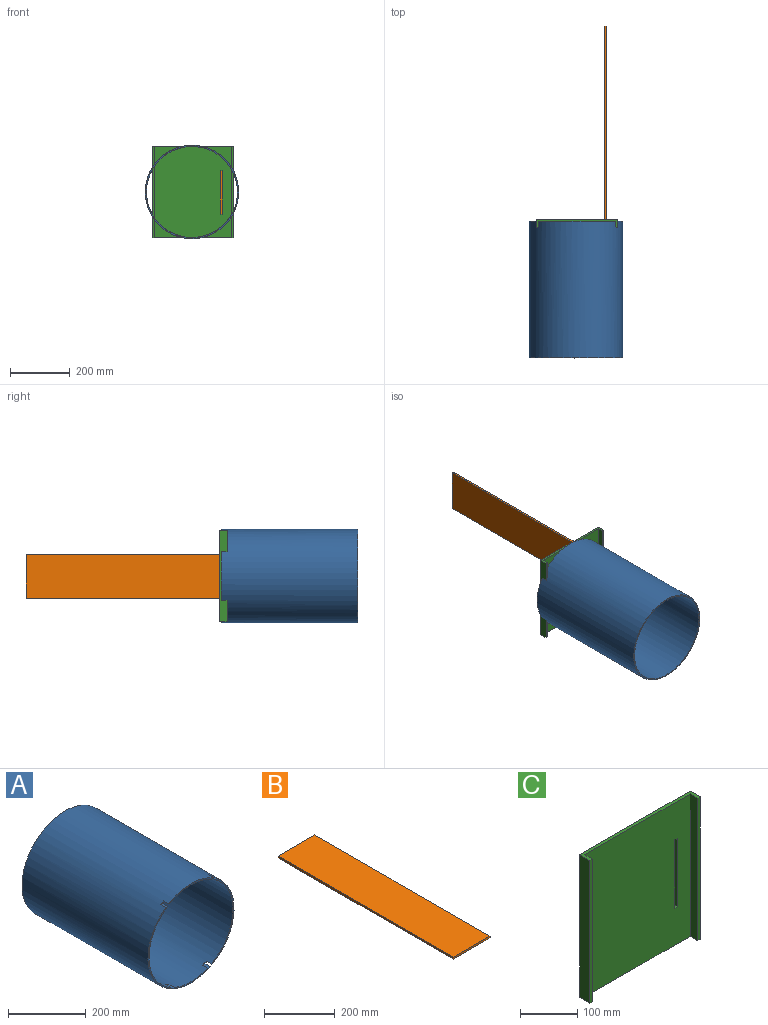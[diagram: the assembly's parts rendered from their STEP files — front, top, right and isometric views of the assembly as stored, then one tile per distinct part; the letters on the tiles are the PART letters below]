
ASSEMBLY  parts=3 mates=2
PART A: 19 faces, bbox 312.4x457.2x312.4 mm
  f0: cylinder r=152.4mm len=457.2mm, axis (0,1,0), area 436781.8mm2, adj f1,f2,f3,f4,f6,f7,f8,f9
  f1: plane 162.72x22.86mm, normal (0,-1,0), area 619.8mm2, adj f0,f5,f8,f16
  f2: plane 260.35x82.43mm, normal (0,-1,0), area 1182mm2, adj f0,f5,f11,f17
  f3: plane 260.35x82.43mm, normal (0,-1,0), area 1182mm2, adj f0,f5,f9,f13
  f4: plane 139.79x16.51mm, normal (0,-1,0), area 515.4mm2, adj f0,f5,f10,f14
  f5: cylinder r=156.21mm len=457.2mm, axis (0,1,0), area 447802.3mm2, adj f1,f2,f3,f4,f6,f7,f8,f9
  f6: plane 312.42x312.42mm, normal (0,1,0), area 3693.9mm2, adj f0,f5
  f7: plane 17.17x6.35mm, normal (0,-1,0), area 45.2mm2, adj f0,f5,f8,f9
  f8: plane 19.05x7.58mm, normal (0,0,-1), area 144.4mm2, adj f0,f1,f5,f7
  f9: plane 19.05x6.71mm, normal (0,0,1), area 127.9mm2, adj f0,f3,f5,f7
  f10: plane 19.05x8.99mm, normal (0,0,1), area 171.2mm2, adj f0,f4,f5,f12
  f11: plane 19.05x7.58mm, normal (0,0,-1), area 144.4mm2, adj f0,f2,f5,f12
  f12: plane 20.45x6.35mm, normal (0,-1,0), area 52.2mm2, adj f0,f5,f10,f11
  f13: plane 19.05x7.58mm, normal (0,0,-1), area 144.4mm2, adj f0,f3,f5,f15
  f14: plane 19.05x8.99mm, normal (0,0,1), area 171.2mm2, adj f0,f4,f5,f15
  f15: plane 20.45x6.35mm, normal (0,-1,0), area 52.2mm2, adj f0,f5,f13,f14
  f16: plane 19.05x7.58mm, normal (0,0,-1), area 144.4mm2, adj f0,f1,f5,f18
  f17: plane 19.05x6.71mm, normal (0,0,1), area 127.9mm2, adj f0,f2,f5,f18
  f18: plane 17.17x6.35mm, normal (0,-1,0), area 45.2mm2, adj f0,f5,f16,f17
PART B: 8 faces, bbox 146.1x698.5x6.4 mm
  f0: plane 698.5x6.35mm, normal (-1,0,0), area 4422.6mm2, adj f1,f3,f4,f5,f6,f7
  f1: plane 647.7x146.05mm, normal (0,0,-1), area 94596.6mm2, adj f0,f2,f4,f7
  f2: plane 698.5x6.35mm, normal (1,0,0), area 4422.6mm2, adj f1,f3,f4,f5,f6,f7
  f3: plane 698.5x146.05mm, normal (0,0,1), area 102015.9mm2, adj f0,f2,f4,f5
  f4: plane 146.05x6.35mm, normal (0,-1,0), area 927.4mm2, adj f0,f1,f2,f3
  f5: plane 146.05x6.1mm, normal (0,1,0), area 890.3mm2, adj f0,f2,f3,f6
  f6: plane 146.05x50.8mm, normal (0,0,-1), area 7419.3mm2, adj f0,f2,f5,f7
  f7: plane 146.05x0.25mm, normal (0,1,0), area 37.1mm2, adj f0,f1,f2,f6
PART C: 14 faces, bbox 273.1x25.4x304.8 mm
  f0: plane 304.8x260.35mm, normal (0,-1,0), area 78464.4mm2, adj f2,f4,f6,f8,f10,f11,f12,f13
  f1: plane 304.8x25.4mm, normal (-1,0,0), area 7741.9mm2, adj f2,f4,f5,f7
  f2: plane 273.05x25.4mm, normal (0,0,-1), area 1975.8mm2, adj f0,f1,f3,f5,f6,f7,f8,f9
  f3: plane 304.8x25.4mm, normal (1,0,0), area 7741.9mm2, adj f2,f4,f5,f9
  f4: plane 273.05x25.4mm, normal (0,0,1), area 1975.8mm2, adj f0,f1,f3,f5,f6,f7,f8,f9
  f5: plane 304.8x273.05mm, normal (0,1,0), area 82335.3mm2, adj f1,f2,f3,f4,f10,f11,f12,f13
  f6: plane 304.8x19.05mm, normal (1,0,0), area 5806.4mm2, adj f0,f2,f4,f7
  f7: plane 304.8x6.35mm, normal (0,-1,0), area 1935.5mm2, adj f1,f2,f4,f6
  f8: plane 304.8x19.05mm, normal (-1,0,0), area 5806.4mm2, adj f0,f2,f4,f9
  f9: plane 304.8x6.35mm, normal (0,-1,0), area 1935.5mm2, adj f2,f3,f4,f8
  f10: plane 146.05x6.35mm, normal (-1,0,0), area 927.4mm2, adj f0,f5,f11,f13
  f11: plane 6.35x6.1mm, normal (0,0,1), area 38.7mm2, adj f0,f5,f10,f12
  f12: plane 146.05x6.35mm, normal (1,0,0), area 927.4mm2, adj f0,f5,f11,f13
  f13: plane 6.35x6.1mm, normal (0,0,-1), area 38.7mm2, adj f0,f5,f10,f12
PLACE A rot(axis=(0.71,0,-0.71),180deg) t=(-571.22,-313.97,-327.83)mm
PLACE B rot(axis=(0.71,0,0.71),180deg) t=(-475.72,98.78,-402.22)mm
PLACE C t=(-704.57,149.58,-481.6)mm
MATE fastened A.f16 <-> C.f1  axis (1,0,0) through (-704.57,133.71,-405.4)mm
MATE fastened B.f7 <-> C.f5  axis (0,-1,0) through (-475.72,149.58,-329.2)mm
